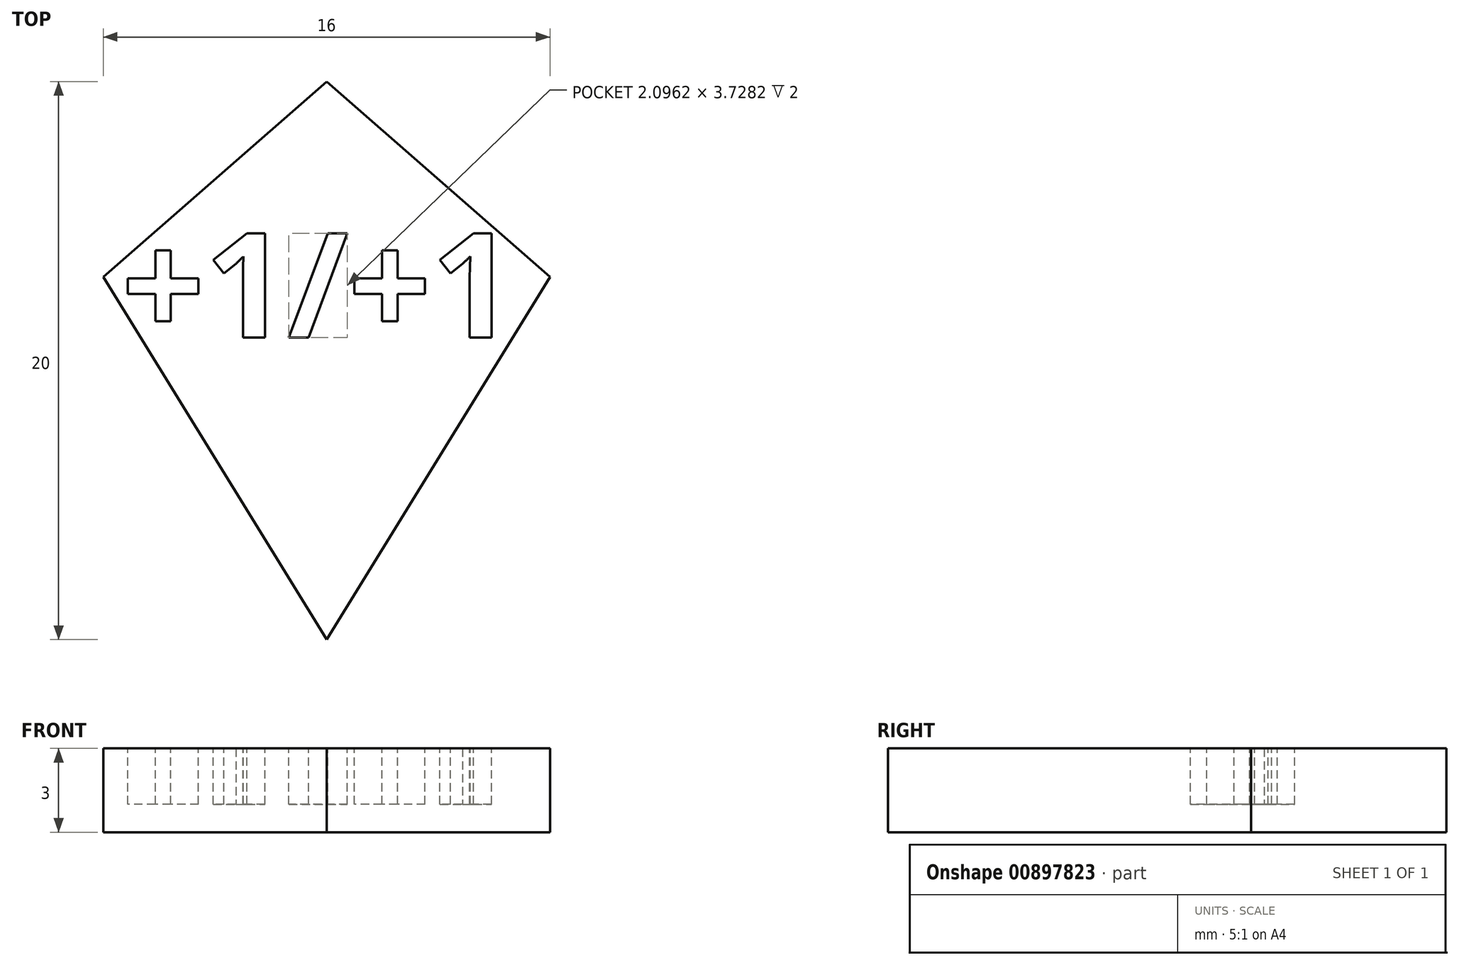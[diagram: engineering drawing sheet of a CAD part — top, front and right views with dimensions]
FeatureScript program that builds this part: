
annotation { "Feature Type Name" : "Feature", "Feature Type Description" : "" }
export const myFeature = defineFeature(function(context is Context, id is Id, definition is map)
    precondition{}
    {
        {
            var Q0;
            Q0=qCreatedBy(makeId("Top.planeOp"),FACE);
            var sketch = newSketch(context, id + "F0", { "sketchPlane" : qUnion([Q0])});
            skLineSegment(sketch, "E0", {"start": v(0, 0) * mm, "end": v(0, 7) * mm});
            skLineSegment(sketch, "E1", {"start": v(0, 7) * mm, "end": v(8, 0) * mm});
            skLineSegment(sketch, "E2", {"start": v(8, 0) * mm, "end": v(0, -13) * mm});
            skLineSegment(sketch, "E3", {"start": v(0, -13) * mm, "end": v(-8, 0) * mm});
            skLineSegment(sketch, "E4", {"start": v(-8, 0) * mm, "end": v(0, 7) * mm});
            skSolve(sketch);
        }
        {
            var Q0;
            Q0=makeQuery(id+"F0.imprint","IMPRINT",FACE,{"disambiguationData":[TD([[makeQuery(id+"F0.imprint","IMPRINT",EDGE,{"derivedFrom":sQuery(id+"F0.wireOp",EDGE,"E1")}),-1.0]])]});
            extrude(context, id + "F1", {"entities" : qUnion([Q0]), "depth" : 3 * mm, "offsetDistance" : 25 * mm});
        }
        {
            var Q0;
            Q0=makeQuery(id+"F1.opExtrude","CAP_FACE",FACE,{"disambiguationData":[OSD([sQuery(id+"F0.wireOp",EDGE,"E1"),sQuery(id+"F0.wireOp",EDGE,"E2"),sQuery(id+"F0.wireOp",EDGE,"E3"),sQuery(id+"F0.wireOp",EDGE,"E4")])],"isStart":false});
            var sketch = newSketch(context, id + "F2", { "sketchPlane" : qUnion([Q0])});
            skText(sketch, "E5", { "text": "+1/+1", "fontName": "OpenSans-Bold.ttf"});
            const initialGuessF2  = {"E5": [-0.00735, -0.00217, 1, 0, 0.00376]};
            skSetInitialGuess(sketch, initialGuessF2);
            skSolve(sketch);
        }
        {
            var Q0;
            Q0 = qSketchRegion(id + "F2", true);
            extrude(context, id + "F3", {"entities" : qUnion([Q0]), "operationType" : NewBodyOperationType.REMOVE, "oppositeDirection" : true, "depth" : 2 * mm, "offsetDistance" : 25 * mm});
        }
    });
